# Revit family: KEUCO_14980010037
name_source: partatom
category: Allgemeines Modell
revit_build: Autodesk Revit 2016 (Build: 20150220_1215(x64)
units: mm (PartAtom-declared; Revit-internal decimal feet)

## family parameters
Arbeitsebenenbasiert = Ja
Beim Laden mit Abzugskörper schneiden = Nein
Bemaßung runder Anschluss = Durchmesser verwenden
Gemeinsam genutzt = Nein
Immer vertikal = Nein
Kann Basisbauteil für Bewehrung sein = Nein
Raumberechnungspunkt = Nein
Teiletyp = Normal

## types (9) — shared parameters
Beschreibung = zur Wandmontage
Sitz nach oben klappbar
Gewicht = 0.522
Hersteller = KEUCO
Kategorie = ACC
Länge = 363 mm  [stored 1.19094 ft]
Serie = Plan
Tiefe = 378 mm  [stored 1.24016 ft]
URL = https://www.keuco.com
Verwendung = DU
Vorgabe-Ansicht = 1219 mm

## per-type parameters (varying)
| type | Ausschreibungstext | Material Regal | Rahmen Material |
| 14980010037 | KEUCO PLAN Klappsitz 14980010037
Schwarzgrauer Klappsitz (RAL 7021) 
aus Polypropylen in ästhetischem, funktionalem Design, 
zur Wandmontage, für sicheres Sitzen im Duschbereich
Wandhalter und Sitzträger als Design-Element hochglanzverchromt
antistatisch, leichte Reinigung
nach oben klappbarer Sitz, belastbar bis 110 kg
Breite 363 mm, Länge der Sitzfläche 310 mm
Ausladung 378 mm
Der Sitz wird verdeckt angebracht 
TÜVRheinland-Zertifizierung beantragt
Das Befestigungsmaterial ist separat zu bestellen!

Zur Montage (je nach Ankergrund/Mauerwerk) unbedingt erforderlich:

1 x Befestigungs-Set 3 (Artikel-Nr. 34992000100)
oder
1 x Befestigungs-Set 6 (Artikel-Nr. 34992000200)
oder
1 x Befestigungs-Set 9 (Artikel-Nr. 34995000200)
oder
1 x Befestigungs-Set 11 (Artikel-Nr. 34997000100) | Schwarzgrau (RAL 7021) | Verchromt |
| 14980010038 | KEUCO PLAN Klappsitz 14980010038
Lichtgrauer Klappsitz (RAL 7035) aus Polypropylen 
in ästhetischem, funktionalem Design, zur Wandmontage
für sicheres Sitzen im Duschbereich
Wandhalter und Sitzträger als Design-Element hochglanzverchromt.
antistatisch, leichte Reinigung
nach oben klappbarer Sitz, belastbar bis 110 kg
Breite 363 mm, Länge der Sitzfläche 310 mm
Ausladung 378 mm
Der Sitz wird verdeckt angebracht 
TÜVRheinland-Zertifizierung beantragt
Das Befestigungsmaterial ist separat zu bestellen!

Zur Montage (je nach Ankergrund/Mauerwerk) unbedingt erforderlich:

1 x Befestigungs-Set 3 (Artikel-Nr. 34992000100)
oder
1 x Befestigungs-Set 6 (Artikel-Nr. 34992000200)
oder
1 x Befestigungs-Set 9 (Artikel-Nr. 34995000200)
oder
1 x Befestigungs-Set 11 (Artikel-Nr. 34997000100) | Weiß (RAL 9010) | Verchromt |
| 14980010051 | KEUCO PLAN Klappsitz 14980010051
Weißer Klappsitz (RAL 9010) aus Polypropylen 
in ästhetischem, funktionalem Design, zur Wandmontage
für sicheres Sitzen im Duschbereich
Wandhalter und Sitzträger als Design-Element hochglanzverchromt.
antistatisch, leichte Reinigung
nach oben klappbarer Sitz, belastbar bis 110 kg
Breite 363 mm, Länge der Sitzfläche 310 mm
Ausladung 378 mm
Der Sitz wird an angebracht 
TÜVRheinland-Zertifizierung beantragt
Das Befestigungsmaterial ist separat zu bestellen!

Zur Montage (je nach Ankergrund/Mauerwerk) unbedingt erforderlich:

1 x Befestigungs-Set 3 (Artikel-Nr. 34992000100)
oder
1 x Befestigungs-Set 6 (Artikel-Nr. 34992000200)
oder
1 x Befestigungs-Set 9 (Artikel-Nr. 34995000200)
oder
1 x Befestigungs-Set 11 (Artikel-Nr. 34997000100) | Weiß (RAL 9010) | Verchromt |
| 14980070037 | KEUCO PLAN Klappsitz 14980070037
Schwarzgrauer Klappsitz (RAL 7021) aus Polypropylen 
in ästhetischem, funktionalem Design, zur Wandmontage
für sicheres Sitzen im Duschbereich
Wandhalter und Sitzträger als Design-Element in Edelstahl-finish
antistatisch, leichte Reinigung
nach oben klappbarer Sitz, belastbar bis 110 kg
Breite 363 mm, Länge der Sitzfläche 310 mm
Ausladung 378 mm
Der Sitz wird an angebracht 
TÜVRheinland-Zertifizierung beantragt
Das Befestigungsmaterial ist separat zu bestellen!

Zur Montage (je nach Ankergrund/Mauerwerk) unbedingt erforderlich:

1 x Befestigungs-Set 3 (Artikel-Nr. 34992000100)
oder
1 x Befestigungs-Set 6 (Artikel-Nr. 34992000200)
oder
1 x Befestigungs-Set 9 (Artikel-Nr. 34995000200)
oder
1 x Befestigungs-Set 11 (Artikel-Nr. 34997000100) | Schwarzgrau (RAL 7021) | Edelstahl |
| 14980070038 | KEUCO PLAN Klappsitz 14980070038
Lichtgrauer Klappsitz (RAL 7035) aus Polypropylen 
in ästhetischem, funktionalem Design, zur Wandmontage
für sicheres Sitzen im Duschbereich
Wandhalter und Sitzträger als Design-Element in Edelstahl-finish
antistatisch, leichte Reinigung
nach oben klappbarer Sitz, belastbar bis 110 kg
Breite 363 mm, Länge der Sitzfläche 310 mm
Ausladung 378 mm
Der Sitz wird verdeckt angebracht 
TÜVRheinland-Zertifizierung beantragt
Das Befestigungsmaterial ist separat zu bestellen!

Zur Montage (je nach Ankergrund/Mauerwerk) unbedingt erforderlich:

1 x Befestigungs-Set 3 (Artikel-Nr. 34992000100)
oder
1 x Befestigungs-Set 6 (Artikel-Nr. 34992000200)
oder
1 x Befestigungs-Set 9 (Artikel-Nr. 34995000200)
oder
1 x Befestigungs-Set 11 (Artikel-Nr. 34997000100) | Lichtgrau (RAL 7035) | Edelstahl |
| 14980070051 | KEUCO PLAN Klappsitz 14980070051
Weißer Klappsitz (RAL 9010) aus Polypropylen 
in ästhetischem, funktionalem Design, zur Wandmontage
für sicheres Sitzen im Duschbereich
Wandhalter und Sitzträger als Design-Element in Edelstahl-finish
antistatisch, leichte Reinigung
nach oben klappbarer Sitz, belastbar bis 110 kg
Breite 363 mm, Länge der Sitzfläche 310 mm
Ausladung 378 mm
Der Sitz wird verdeckt angebracht 
TÜVRheinland-Zertifizierung beantragt
Das Befestigungsmaterial ist separat zu bestellen!

Zur Montage (je nach Ankergrund/Mauerwerk) unbedingt erforderlich:

1 x Befestigungs-Set 3 (Artikel-Nr. 34992000100)
oder
1 x Befestigungs-Set 6 (Artikel-Nr. 34992000200)
oder
1 x Befestigungs-Set 9 (Artikel-Nr. 34995000200)
oder
1 x Befestigungs-Set 11 (Artikel-Nr. 34997000100) | Weiß (RAL 9010) | Edelstahl |
| 14980170037 | KEUCO PLAN Klappsitz 14980170037
Schwarzgrauer Klappsitz (RAL 7021) aus Polypropylen 
in ästhetischem, funktionalem Design, zur Wandmontage
für sicheres Sitzen im Duschbereich
Wandhalter und Sitzträger als Design-Element 
aus silber-eloxiertem Aluminium (E6 EV1)
antistatisch, leichte Reinigung
nach oben klappbarer Sitz, belastbar bis 110 kg
Breite 363 mm, Länge der Sitzfläche 310 mm
Ausladung 378 mm
Der Sitz wird verdeckt angebracht 
TÜVRheinland-Zertifizierung beantragt
Das Befestigungsmaterial ist separat zu bestellen!

Zur Montage (je nach Ankergrund/Mauerwerk) unbedingt erforderlich:

1 x Befestigungs-Set 3 (Artikel-Nr. 34992000100)
oder
1 x Befestigungs-Set 6 (Artikel-Nr. 34992000200)
oder
1 x Befestigungs-Set 9 (Artikel-Nr. 34995000200)
oder
1 x Befestigungs-Set 11 (Artikel-Nr. 34997000100) | Schwarzgrau (RAL 7021) | Aluminium silber-eloxiert (E6 EV1) |
| 14980170038 | KEUCO PLAN Klappsitz 14980170038
Lichtgrauer Klappsitz (RAL 7035) aus Polypropylen 
in ästhetischem, funktionalem Design, zur Wandmontage
für sicheres Sitzen im Duschbereich
Wandhalter und Sitzträger als Design Element 
aus silber-eloxiertem Aluminium (E6 EV1)
antistatisch, leichte Reinigung
nach oben klappbarer Sitz, belastbar bis 110 kg
Breite 363 mm, Länge der Sitzfläche 310 mm
Ausladung 378 mm
Der Sitz wird verdeckt angebracht 
TÜVRheinland-Zertifizierung beantragt
Das Befestigungsmaterial ist separat zu bestellen!

Zur Montage (je nach Ankergrund/Mauerwerk) unbedingt erforderlich:

1 x Befestigungs-Set 3 (Artikel-Nr. 34992000100)
oder
1 x Befestigungs-Set 6 (Artikel-Nr. 34992000200)
oder
1 x Befestigungs-Set 9 (Artikel-Nr. 34995000200)
oder
1 x Befestigungs-Set 11 (Artikel-Nr. 34997000100) | Lichtgrau (RAL 7035) | Aluminium silber-eloxiert (E6 EV1) |
| 14980170051 | KEUCO PLAN Klappsitz 14980170051
Weißer Klappsitz (RAL 9010) aus Polypropylen 
in ästhetischem, funktionalem Design, zur Wandmontage
für sicheres Sitzen im Duschbereich
Wandhalter und Sitzträger als Design-Element 
aus silber-eloxiertem Aluminium (E6 EV1)
antistatisch, leichte Reinigung
nach oben klappbarer Sitz, belastbar bis 110 kg
Breite 363 mm, Länge der Sitzfläche 310 mm
Ausladung 378 mm
Der Sitz wird verdeckt angebracht
TÜVRheinland-Zertifizierung beantragt
Das Befestigungsmaterial ist separat zu bestellen!

Zur Montage (je nach Ankergrund/Mauerwerk) unbedingt erforderlich:

1 x Befestigungs-Set 3 (Artikel-Nr. 34992000100)
oder
1 x Befestigungs-Set 6 (Artikel-Nr. 34992000200)
oder
1 x Befestigungs-Set 9 (Artikel-Nr. 34995000200)
oder
1 x Befestigungs-Set 11 (Artikel-Nr. 34997000100) | Weiß (RAL 9010) | Aluminium silber-eloxiert (E6 EV1) |

note: column(s) folded — value = type name in every type: Artikelnummer

note: [stored X ft] marks values corroborated as IEEE doubles in the binary element streams (Revit-internal decimal feet)

## geometry (parser evidence)
native form markers: Blend x2, Sweep x3
no freeform markers — native parametric forms only
